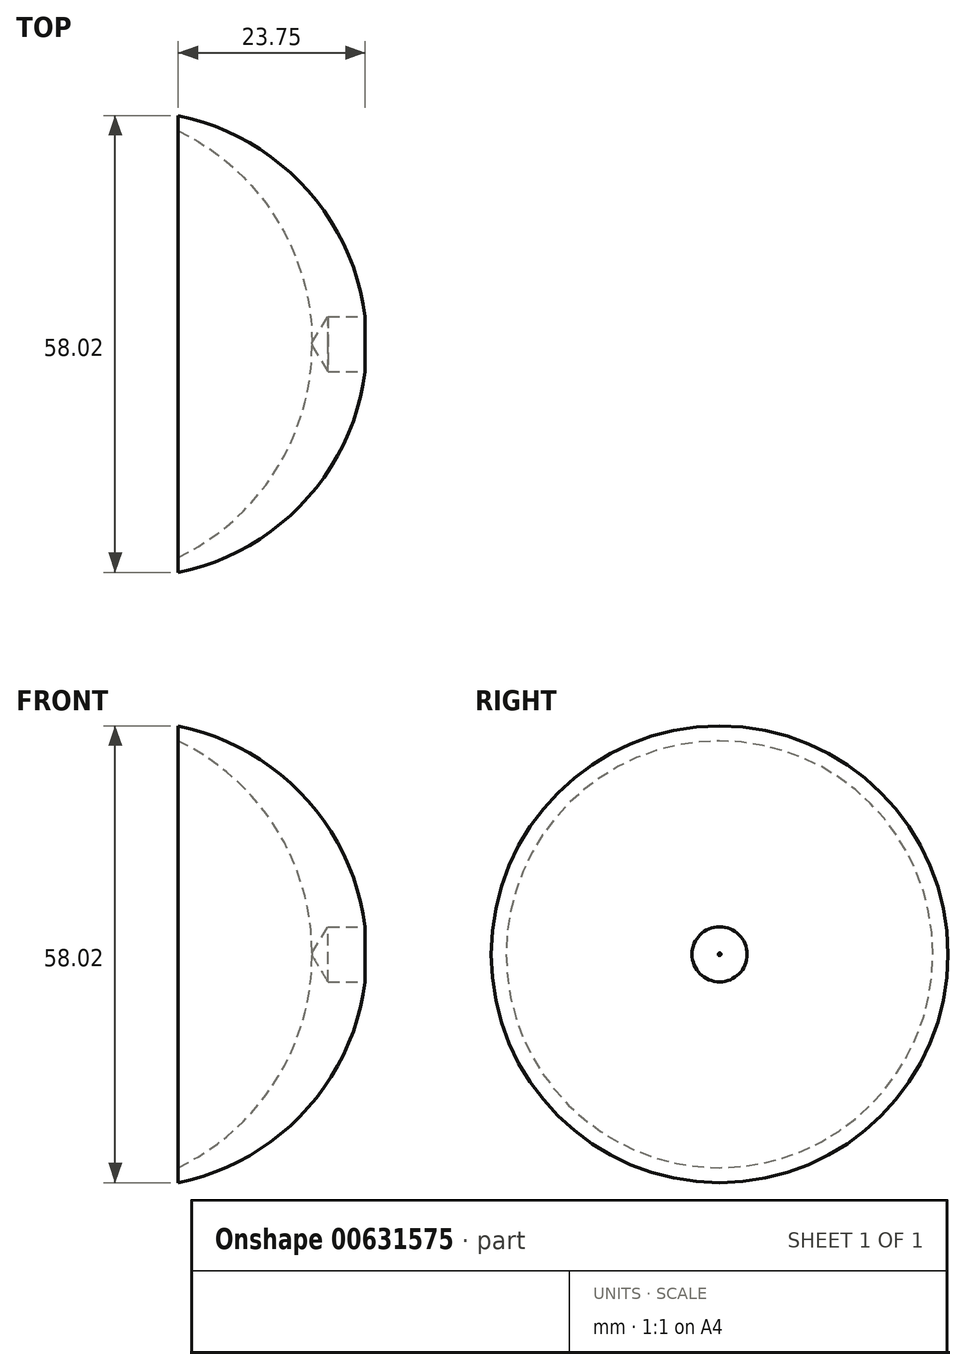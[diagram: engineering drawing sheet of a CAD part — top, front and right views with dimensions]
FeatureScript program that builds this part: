
annotation { "Feature Type Name" : "Feature", "Feature Type Description" : "" }
export const myFeature = defineFeature(function(context is Context, id is Id, definition is map)
    precondition{}
    {
        {
            var Q0;
            Q0=qCreatedBy(makeId("Front.planeOp"),FACE);
            var sketch = newSketch(context, id + "F0", { "sketchPlane" : qUnion([Q0])});
            skArc(sketch, "E0", {"start": v(0, 0) * mm, "mid": v(-6.88, 18.74) * mm, "end": v(-24, 29.01) * mm});
            skArc(sketch, "E1", {"start": v(-7, 0) * mm, "mid": v(-11.59, 16) * mm, "end": v(-24, 27.1) * mm});
            skLineSegment(sketch, "E2", {"start": v(-7, 0) * mm, "end": v(0, 0) * mm});
            skLineSegment(sketch, "E3", {"start": v(-24, 29.01) * mm, "end": v(-24, 27.1) * mm});
            skSolve(sketch);
        }
        {
            var Q0;
            Q0=makeQuery(id+"F0.imprint","IMPRINT",FACE,{"disambiguationData":[TD([[makeQuery(id+"F0.imprint","IMPRINT",EDGE,{"derivedFrom":sQuery(id+"F0.wireOp",EDGE,"E0")}),1.0]])]});
            var Q1;
            Q1=sQuery(id+"F0.wireOp",EDGE,"E2");
            revolve(context, id + "F1", {"entities" : qUnion([Q0]), "axis" : qUnion([Q1]), "revolveType" : RevolveType.FULL});
        }
        {
            var Q0;
            Q0=qCreatedBy(makeId("Right.planeOp"),FACE);
            var sketch = newSketch(context, id + "F2", { "sketchPlane" : qUnion([Q0])});
            skCircle(sketch, "E4", {"center": v(0, 0) * mm, "radius": 167.18 * mm});
            skSolve(sketch);
        }
        {
            var Q0;
            Q0=sQuery(id+"F2.wireOp",VERTEX,"E4.center");
            var Q1;
            Q1=makeQuery(id+"F1.opRevolve","SWEPT_BODY",BODY,{"disambiguationData":[OSD([sQuery(id+"F0.wireOp",EDGE,"E0"),sQuery(id+"F0.wireOp",EDGE,"E1"),sQuery(id+"F0.wireOp",EDGE,"E2"),sQuery(id+"F0.wireOp",EDGE,"E3")])]});
            hole(context, id + "F3", {"style" : HoleStyle.SIMPLE, "endStyle" : HoleEndStyle.BLIND, "holeDiameter" : 7 * mm, "majorDiameter" : 5 * mm, "holeDepth" : 5 * mm, "isTappedThrough" : true, "tappedDepth" : 12.7 * mm, "tapClearance" : 3, "startFromSketch" : true, "locations" : qUnion([Q0]), "scope" : qUnion([Q1])});
        }
    });
